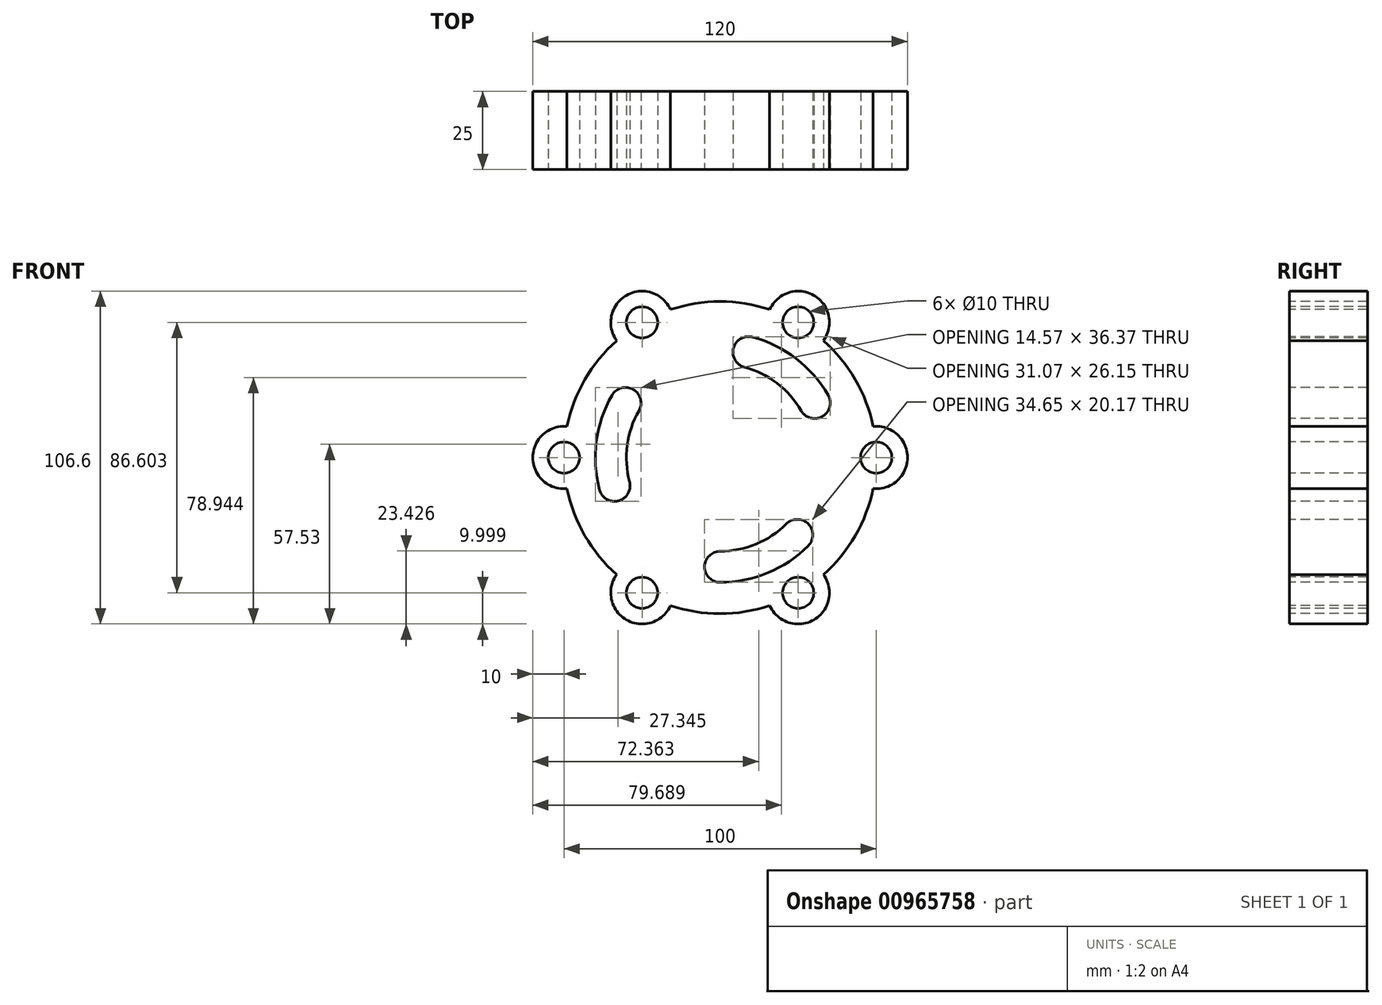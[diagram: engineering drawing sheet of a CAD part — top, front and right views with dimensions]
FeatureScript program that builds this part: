
annotation { "Feature Type Name" : "Feature", "Feature Type Description" : "" }
export const myFeature = defineFeature(function(context is Context, id is Id, definition is map)
    precondition{}
    {
        {
            var Q0;
            Q0=qCreatedBy(makeId("Front.planeOp"),FACE);
            var sketch = newSketch(context, id + "F0", { "sketchPlane" : qUnion([Q0])});
            skArc(sketch, "E0", {"start": v(-49, -9.95) * mm, "mid": v(50, 0) * mm, "end": v(-49, 9.95) * mm});
            skArc(sketch, "E1", {"start": v(-49, 9.95) * mm, "mid": v(-60, 0) * mm, "end": v(-49, -9.95) * mm});
            skCircle(sketch, "E2", {"center": v(-50, 0) * mm, "radius": 5 * mm});
            skCircle(sketch, "E3.1.0", {"center": v(-25, -43.3) * mm, "radius": 5 * mm});
            skArc(sketch, "E3.1.1", {"start": v(-33.12, -37.46) * mm, "mid": v(-30, -51.96) * mm, "end": v(-15.88, -47.41) * mm});
            skCircle(sketch, "E3.2.0", {"center": v(25, -43.3) * mm, "radius": 5 * mm});
            skArc(sketch, "E3.2.1", {"start": v(15.88, -47.41) * mm, "mid": v(30, -51.96) * mm, "end": v(33.12, -37.46) * mm});
            skCircle(sketch, "E3.3.0", {"center": v(50, 0) * mm, "radius": 5 * mm});
            skArc(sketch, "E3.3.1", {"start": v(49, -9.95) * mm, "mid": v(60, 0) * mm, "end": v(49, 9.95) * mm});
            skCircle(sketch, "E3.4.0", {"center": v(25, 43.3) * mm, "radius": 5 * mm});
            skArc(sketch, "E3.4.1", {"start": v(33.12, 37.46) * mm, "mid": v(30, 51.96) * mm, "end": v(15.88, 47.41) * mm});
            skCircle(sketch, "E3.5.0", {"center": v(-25, 43.3) * mm, "radius": 5 * mm});
            skArc(sketch, "E3.5.1", {"start": v(-15.88, 47.41) * mm, "mid": v(-30, 51.96) * mm, "end": v(-33.12, 37.46) * mm});
            skSolve(sketch);
        }
        {
            var Q0;
            {var subQ4=sQuery(id+"F0.wireOp",EDGE,"E1");Q0=makeQuery(id+"F0.imprint","IMPRINT",FACE,{"disambiguationData":[TD([[makeQuery(id+"F0.imprint","IMPRINT",EDGE,{"derivedFrom":subQ4}),1.0]])]});}
            var sketch = newSketch(context, id + "F1", { "sketchPlane" : qUnion([Q0])});
            skArc(sketch, "E4", {"start": v(10.38, 38.59) * mm, "mid": v(4.28, 35.08) * mm, "end": v(7.8, 28.98) * mm});
            skArc(sketch, "E5", {"start": v(25.99, 15.01) * mm, "mid": v(32.78, 13.2) * mm, "end": v(34.6, 20) * mm});
            skArc(sketch, "E6", {"start": v(10.38, 38.59) * mm, "mid": v(24.53, 31.54) * mm, "end": v(34.84, 19.56) * mm});
            skArc(sketch, "E7", {"start": v(7.8, 28.98) * mm, "mid": v(18.28, 23.8) * mm, "end": v(25.99, 15.01) * mm});
            skArc(sketch, "E8.1.0", {"start": v(-38.6, -10.3) * mm, "mid": v(-32.52, -13.83) * mm, "end": v(-29, -7.74) * mm});
            skArc(sketch, "E8.1.1", {"start": v(-38.6, -10.3) * mm, "mid": v(-39.58, 5.47) * mm, "end": v(-34.36, 20.4) * mm});
            skArc(sketch, "E8.1.2", {"start": v(-29, -7.74) * mm, "mid": v(-29.75, 3.93) * mm, "end": v(-26, 15) * mm});
            skArc(sketch, "E8.1.3", {"start": v(-26, 15) * mm, "mid": v(-27.82, 21.8) * mm, "end": v(-34.61, 19.97) * mm});
            skArc(sketch, "E8.2.0", {"start": v(28.23, -28.28) * mm, "mid": v(28.24, -21.25) * mm, "end": v(21.2, -21.24) * mm});
            skArc(sketch, "E8.2.1", {"start": v(28.23, -28.28) * mm, "mid": v(15.05, -37.02) * mm, "end": v(-0.48, -39.96) * mm});
            skArc(sketch, "E8.2.2", {"start": v(21.2, -21.24) * mm, "mid": v(11.48, -27.73) * mm, "end": v(0, -30.01) * mm});
            skArc(sketch, "E8.2.3", {"start": v(0, -30.01) * mm, "mid": v(-4.96, -34.99) * mm, "end": v(0.01, -39.96) * mm});
            skSolve(sketch);
        }
        {
            var Q0;
            {var subQ4=sQuery(id+"F0.wireOp",EDGE,"E1");Q0=makeQuery(id+"F0.imprint","IMPRINT",FACE,{"disambiguationData":[TD([[makeQuery(id+"F0.imprint","IMPRINT",EDGE,{"derivedFrom":subQ4}),1.0]])]});}
            var Q1;
            {var subQ0=sQuery(id+"F0.wireOp",EDGE,"E3.5.1");Q1=makeQuery(id+"F0.imprint","IMPRINT",FACE,{"disambiguationData":[TD([[makeQuery(id+"F0.imprint","IMPRINT",EDGE,{"derivedFrom":subQ0}),1.0]])]});}
            var Q2;
            {var subQ0=sQuery(id+"F0.wireOp",EDGE,"E3.4.1");Q2=makeQuery(id+"F0.imprint","IMPRINT",FACE,{"disambiguationData":[TD([[makeQuery(id+"F0.imprint","IMPRINT",EDGE,{"derivedFrom":subQ0}),1.0]])]});}
            var Q3;
            {var subQ0=sQuery(id+"F0.wireOp",EDGE,"E3.3.1");Q3=makeQuery(id+"F0.imprint","IMPRINT",FACE,{"disambiguationData":[TD([[makeQuery(id+"F0.imprint","IMPRINT",EDGE,{"derivedFrom":subQ0}),1.0]])]});}
            var Q4;
            {var subQ0=sQuery(id+"F0.wireOp",EDGE,"E3.2.1");Q4=makeQuery(id+"F0.imprint","IMPRINT",FACE,{"disambiguationData":[TD([[makeQuery(id+"F0.imprint","IMPRINT",EDGE,{"derivedFrom":subQ0}),1.0]])]});}
            var Q5;
            {var subQ0=sQuery(id+"F0.wireOp",EDGE,"E3.1.1");Q5=makeQuery(id+"F0.imprint","IMPRINT",FACE,{"disambiguationData":[TD([[makeQuery(id+"F0.imprint","IMPRINT",EDGE,{"derivedFrom":subQ0}),1.0]])]});}
            extrude(context, id + "F2", {"entities" : qUnion([Q0, Q1, Q2, Q3, Q4, Q5]), "oppositeDirection" : true, "depth" : 25 * mm, "offsetDistance" : 25 * mm});
        }
        {
            var Q0;
            {var subQ0=sQuery(id+"F1.wireOp",EDGE,"E8.1.0");Q0=makeQuery(id+"F1.imprint","IMPRINT",FACE,{"disambiguationData":[TD([[makeQuery(id+"F1.imprint","IMPRINT",EDGE,{"derivedFrom":subQ0}),1.0]])]});}
            var Q1;
            {var subQ0=sQuery(id+"F1.wireOp",EDGE,"E4");Q1=makeQuery(id+"F1.imprint","IMPRINT",FACE,{"disambiguationData":[TD([[makeQuery(id+"F1.imprint","IMPRINT",EDGE,{"derivedFrom":subQ0}),1.0]])]});}
            var Q2;
            {var subQ0=sQuery(id+"F1.wireOp",EDGE,"E8.2.0");Q2=makeQuery(id+"F1.imprint","IMPRINT",FACE,{"disambiguationData":[TD([[makeQuery(id+"F1.imprint","IMPRINT",EDGE,{"derivedFrom":subQ0}),1.0]])]});}
            extrude(context, id + "F3", {"entities" : qUnion([Q0, Q1, Q2]), "operationType" : NewBodyOperationType.REMOVE, "endBound" : BoundingType.THROUGH_ALL, "oppositeDirection" : true, "depth" : 25 * mm, "offsetDistance" : 25 * mm});
        }
    });
